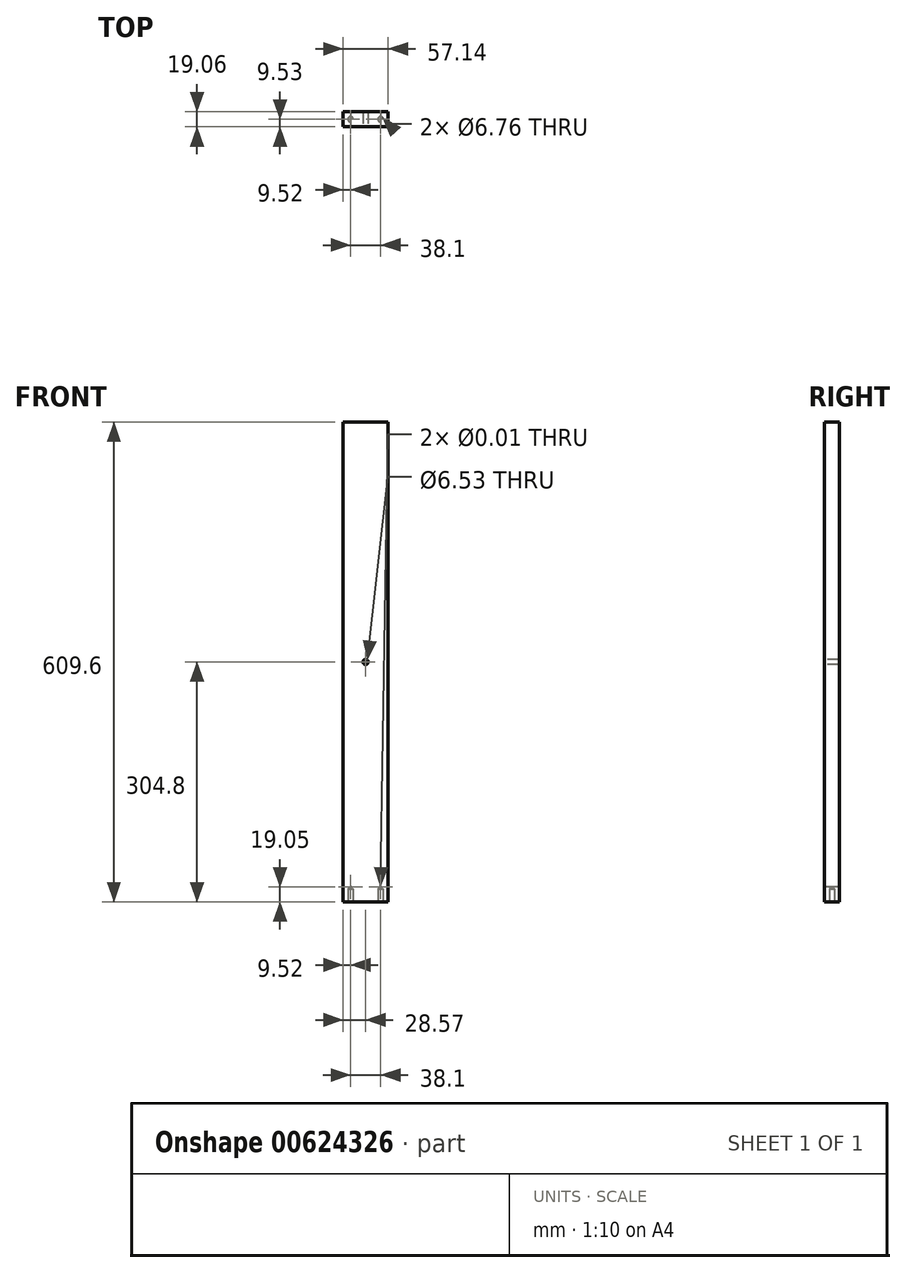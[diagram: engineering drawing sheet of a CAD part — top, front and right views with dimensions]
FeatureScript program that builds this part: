
annotation { "Feature Type Name" : "Feature", "Feature Type Description" : "" }
export const myFeature = defineFeature(function(context is Context, id is Id, definition is map)
    precondition{}
    {
        {
            var Q0;
            Q0=qCreatedBy(makeId("Front.planeOp"),FACE);
            var sketch = newSketch(context, id + "F0", { "sketchPlane" : qUnion([Q0])});
            skLineSegment(sketch, "E0.bottom", {"start": v(-28.57, 304.8) * mm, "end": v(28.58, 304.8) * mm});
            skLineSegment(sketch, "E0.top", {"start": v(-28.58, -304.8) * mm, "end": v(28.57, -304.8) * mm});
            skLineSegment(sketch, "E0.left", {"start": v(-28.57, 304.8) * mm, "end": v(-28.58, -304.8) * mm});
            skLineSegment(sketch, "E0.right", {"start": v(28.58, 304.8) * mm, "end": v(28.58, -304.8) * mm});
            skLineSegment(sketch, "E1", {"start": v(0, 304.8) * mm, "end": v(0, -304.8) * mm, "construction": true});
            skLineSegment(sketch, "E2", {"start": v(-28.57, 0) * mm, "end": v(28.57, 0) * mm, "construction": true});
            skSolve(sketch);
        }
        {
            var Q0;
            Q0=makeQuery(id+"F0.imprint","IMPRINT",FACE,{"disambiguationData":[TD([[makeQuery(id+"F0.imprint","IMPRINT",EDGE,{"derivedFrom":sQuery(id+"F0.wireOp",EDGE,"E0.bottom")}),-1.0]])]});
            extrude(context, id + "F1", {"entities" : qUnion([Q0]), "endBound" : BoundingType.SYMMETRIC, "depth" : 19.05 * mm, "offsetDistance" : 25.4 * mm});
        }
        {
            var Q0;
            Q0=makeQuery(id+"F1.opExtrude","CAP_FACE",FACE,{"disambiguationData":[OSD([sQuery(id+"F0.wireOp",EDGE,"E0.bottom"),sQuery(id+"F0.wireOp",EDGE,"E0.top"),sQuery(id+"F0.wireOp",EDGE,"E0.left"),sQuery(id+"F0.wireOp",EDGE,"E0.right")])],"isStart":false});
            var sketch = newSketch(context, id + "F2", { "sketchPlane" : qUnion([Q0])});
            skLineSegment(sketch, "E3", {"start": v(-28.57, -285.75) * mm, "end": v(28.58, -285.75) * mm, "construction": true});
            skPoint(sketch, "E4", {"position": v(-19.05, -285.75) * mm});
            skPoint(sketch, "E5", {"position": v(19.05, -285.75) * mm});
            skSolve(sketch);
        }
        {
            var Q0;
            Q0=sQuery(id+"F2.wireOp",VERTEX,"E4");
            var Q1;
            Q1=sQuery(id+"F2.wireOp",VERTEX,"E5");
            var Q2;
            Q2=makeQuery(id+"F1.opExtrude","SWEPT_BODY",BODY,{"disambiguationData":[OSD([sQuery(id+"F0.wireOp",EDGE,"E0.bottom"),sQuery(id+"F0.wireOp",EDGE,"E0.top"),sQuery(id+"F0.wireOp",EDGE,"E0.left"),sQuery(id+"F0.wireOp",EDGE,"E0.right")])]});
            hole(context, id + "F3", {"style" : HoleStyle.SIMPLE, "endStyle" : HoleEndStyle.BLIND, "standardTappedOrClearance" : lookupTablePath({ "standard" : "ANSI", "size" : "3/8 (0.38)", "type" : "Drilled" }), "standardBlindInLast" : lookupTablePath({ "standard" : "ANSI", "size" : "3/8", "type" : "Drilled" }), "holeDiameter" : 3 / 203.2 * mm, "majorDiameter" : 6.35 * mm, "holeDepth" : 16.54 * mm, "isTappedThrough" : true, "tappedDepth" : 12.7 * mm, "tapClearance" : 3, "startFromSketch" : true, "locations" : qUnion([Q0, Q1]), "scope" : qUnion([Q2])});
        }
        {
            var Q0;
            Q0=makeQuery(id+"F1.opExtrude","SWEPT_FACE",FACE,{"disambiguationData":[OSD([sQuery(id+"F0.wireOp",EDGE,"E0.top")])]});
            var sketch = newSketch(context, id + "F4", { "sketchPlane" : qUnion([Q0])});
            skLineSegment(sketch, "E6", {"start": v(-28.57, 0) * mm, "end": v(28.58, 0) * mm, "construction": true});
            skPoint(sketch, "E7", {"position": v(-19.05, 0) * mm});
            skPoint(sketch, "E8", {"position": v(19.05, 0) * mm});
            skSolve(sketch);
        }
        {
            var Q0;
            Q0=sQuery(id+"F4.wireOp",VERTEX,"E7");
            var Q1;
            Q1=sQuery(id+"F4.wireOp",VERTEX,"E8");
            var Q2;
            Q2=makeQuery(id+"F1.opExtrude","SWEPT_BODY",BODY,{"disambiguationData":[OSD([sQuery(id+"F0.wireOp",EDGE,"E0.bottom"),sQuery(id+"F0.wireOp",EDGE,"E0.top"),sQuery(id+"F0.wireOp",EDGE,"E0.left"),sQuery(id+"F0.wireOp",EDGE,"E0.right")])]});
            hole(context, id + "F5", {"style" : HoleStyle.SIMPLE, "endStyle" : HoleEndStyle.BLIND, "standardTappedOrClearance" : lookupTablePath({ "standard" : "ANSI", "fit" : "Normal (ASME)", "size" : "1/4", "type" : "Clearance" }), "standardBlindInLast" : lookupTablePath({ "fit" : "Free", "standard" : "ANSI", "size" : "1/4", "type" : "Clearance" }), "holeDiameter" : 6.76 * mm, "majorDiameter" : 6.35 * mm, "holeDepth" : 16.54 * mm, "isTappedThrough" : true, "tappedDepth" : 12.7 * mm, "tapClearance" : 3, "startFromSketch" : true, "locations" : qUnion([Q0, Q1]), "scope" : qUnion([Q2])});
        }
        {
            var Q0;
            Q0=makeQuery(id+"F2.imprint","IMPRINT",FACE,{"disambiguationData":[TD([[makeQuery(id+"F2.imprint","IMPRINT",EDGE,{"derivedFrom":makeQuery(id+"F1.opExtrude","CAP_EDGE",EDGE,{"disambiguationData":[OSD([sQuery(id+"F0.wireOp",EDGE,"E0.bottom")])],"isStart":false})}),-1.0]])]});
            var sketch = newSketch(context, id + "F6", { "sketchPlane" : qUnion([Q0])});
            skPoint(sketch, "E9", {"position": v(0, 0) * mm});
            skSolve(sketch);
        }
        {
            var Q0;
            Q0=sQuery(id+"F6.wireOp",VERTEX,"E9");
            var Q1;
            Q1=makeQuery(id+"F1.opExtrude","SWEPT_BODY",BODY,{"disambiguationData":[OSD([sQuery(id+"F0.wireOp",EDGE,"E0.bottom"),sQuery(id+"F0.wireOp",EDGE,"E0.top"),sQuery(id+"F0.wireOp",EDGE,"E0.left"),sQuery(id+"F0.wireOp",EDGE,"E0.right")])]});
            hole(context, id + "F7", {"style" : HoleStyle.SIMPLE, "endStyle" : HoleEndStyle.THROUGH, "standardTappedOrClearance" : lookupTablePath({ "standard" : "ANSI", "fit" : "Close", "size" : "1/4", "type" : "Clearance" }), "standardBlindInLast" : lookupTablePath({ "fit" : "Close", "standard" : "ANSI", "size" : "1/4", "type" : "Clearance" }), "holeDiameter" : 6.53 * mm, "majorDiameter" : 6.35 * mm, "isTappedThrough" : true, "tappedDepth" : 12.7 * mm, "tapClearance" : 3, "startFromSketch" : true, "locations" : qUnion([Q0]), "scope" : qUnion([Q1])});
        }
    });
